# Revit family: Фобос 05_v1
name_source: partatom
category: Осветительные приборы
units: mm (PartAtom-declared; Revit-internal decimal feet)

## family parameters
Всегда вертикально = Да
Источник света = Да
На основе рабочей плоскости = Нет
Общий = Нет
При загрузке вырезать с полостями = Нет
Размер круглого соединителя = Использовать диаметр
Тип детали = Нормальный
Точка расчета площади = Нет

## types (5) — shared parameters
ADSK_URL страницы изделия = https://www.allfresco.ru
ADSK_Единица измерения = шт.
ADSK_Завод-изготовитель = ALFRESCO
ADSK_Количество фаз = 2
ADSK_Модель = Фобос 05 ДТУ-138-AF
ADSK_Напряжение = 220 В
ADSK_Полная мощность = 0 В·А
ADSK_Ток = 0 А
ADSK_Энергоэффективность = 10 лм/Вт
D_столб_верх = 60 мм
D_столб_низ = 100 мм
H1_светильник = 400 мм
H_дверка = 500 мм
H_конечной точки = 1500 мм
H_фланец = 10 мм
IP Class = IP 67
L_отступ до конечной точки = 1500 мм
L_отступ до центра = 1000 мм
R_дверка_загибы = 10 мм
S_дверка = 70 мм
h_дверка = 400 мм
Блок аварийного питания = Нет
Класс защиты = 1
Класс пожароопасности = F (светильники предназначены для установки непосредственно на поверхность из нормально воспламеняемых материалов)
Климатическая зона = УХЛ1
Короб_Диаметр = 20 мм
Корпус светильника = Сталь, окрашенная, темно-серая
Материал рассеивателя = Светотехнический ПК
Область использования = Парки, скверы, общественные пространства, городская инфраструктура
Полная установленная мощность = 0 В·А
Рассеиватель = Белый_Светодиод
Светофильтр = 16777215
Смещение цветовой температуры при затухании лампы = <Нет>
Таблица выбора = Таблица параметров светильников_par4_v1
Температура эксплуатации = -40 +50
Тип ИС = LED-модуль
Тип КСС = специальная
Тип ПРА = -
Тип продукции = LED-светильник
Угол наклона = 60.00°
Цветоывая температура = 2700-5500
zero-valued in all types: ADSK_Количество фаз числовое, ADSK_Коэффициент мощности

## per-type parameters (varying)
| type | 1 | 2 | 3 | 4 | 5 | ADSK_Артикул | ADSK_Масса | ADSK_Масса_Текст | ADSK_Наименование | ADSK_Номинальная мощность | ADSK_Размер_Высота | ADSK_Фактическая мощность | D_фланец_отверстия | S1_фланец | S2_фланец | Файл фотометрической сетки |
| ДТУ138с14 Светодиодный светильник Фобос 05 ДТУ-138-AF-24Вт-4,0-1-Spot-05-24Вт | Да | Нет | Нет | Нет | Нет | ДТУ138с14 | 31 | 31 | ДТУ138с14 Светодиодный светильник Фобос 05 ДТУ-138-AF-24Вт-4.0-1-Spot-05-24Вт | 24 Вт | 4000 мм | 48 Вт | 18 мм | 230 мм | 190 мм | Spot-05-AF 24W 60°.ies |
| ДТУ138с29 Светодиодный светильник Фобос 05 ДТУ-138-AF-72Вт-5,0-2-Spot-05-36Вт | Нет | Да | Нет | Нет | Нет | ДТУ138с29 | 45 | 45 | ДТУ138с29 Светодиодный светильник Фобос 05 ДТУ-138-AF-72Вт-5.0-2-Spot-05-36Вт | 72 Вт | 5000 мм | 72 Вт | 18 мм | 230 мм | 190 мм | Spot-05-AF 36W 60°.ies |
| ДТУ138с18 Светодиодный светильник Фобос 05 ДТУ-138-AF-72Вт-5,0-3-Spot-05-24Вт | Нет | Нет | Да | Нет | Нет | ДТУ138с18 | 50 | 50 | ДТУ138с18 Светодиодный светильник Фобос 05 ДТУ-138-AF-72Вт-5.0-3-Spot-05-24Вт | 72 Вт | 5000 мм | 72 Вт | 18 мм | 230 мм | 190 мм | Spot-05-AF 24W 60°.ies |
| ДТУ138с131 Светодиодный светильник Фобос 05 ДТУ-138-AF-216Вт-6,0-4-Spot-05-54Вт | Нет | Нет | Нет | Да | Нет | ДТУ138с131 | 62 | 62 | ДТУ138с131 Светодиодный светильник Фобос 05 ДТУ-138-AF-216Вт-6.0-4-Spot-05-54Вт | 216 Вт | 6000 мм | 216 Вт | 22 мм | 280 мм | 200 мм | Spot-05-AF 54W 60°.ies |
| ДТУ138с113 Светодиодный светильник Фобос 05 ДТУ-138-AF-360Вт-6,0-5-Spot-05-72Вт | Нет | Нет | Нет | Нет | Да | ДТУ138с113 | 67 | 67 | ДТУ138с113 Светодиодный светильник Фобос 05 ДТУ-138-AF-360Вт-6.0-5-Spot-05-72Вт | 360 Вт | 6000 мм | 360 Вт | 22 мм | 280 мм | 200 мм | Spot-05-AF 72W 60°.ies |

## geometry (parser evidence)
native form markers: Blend x2
no freeform markers — native parametric forms only
